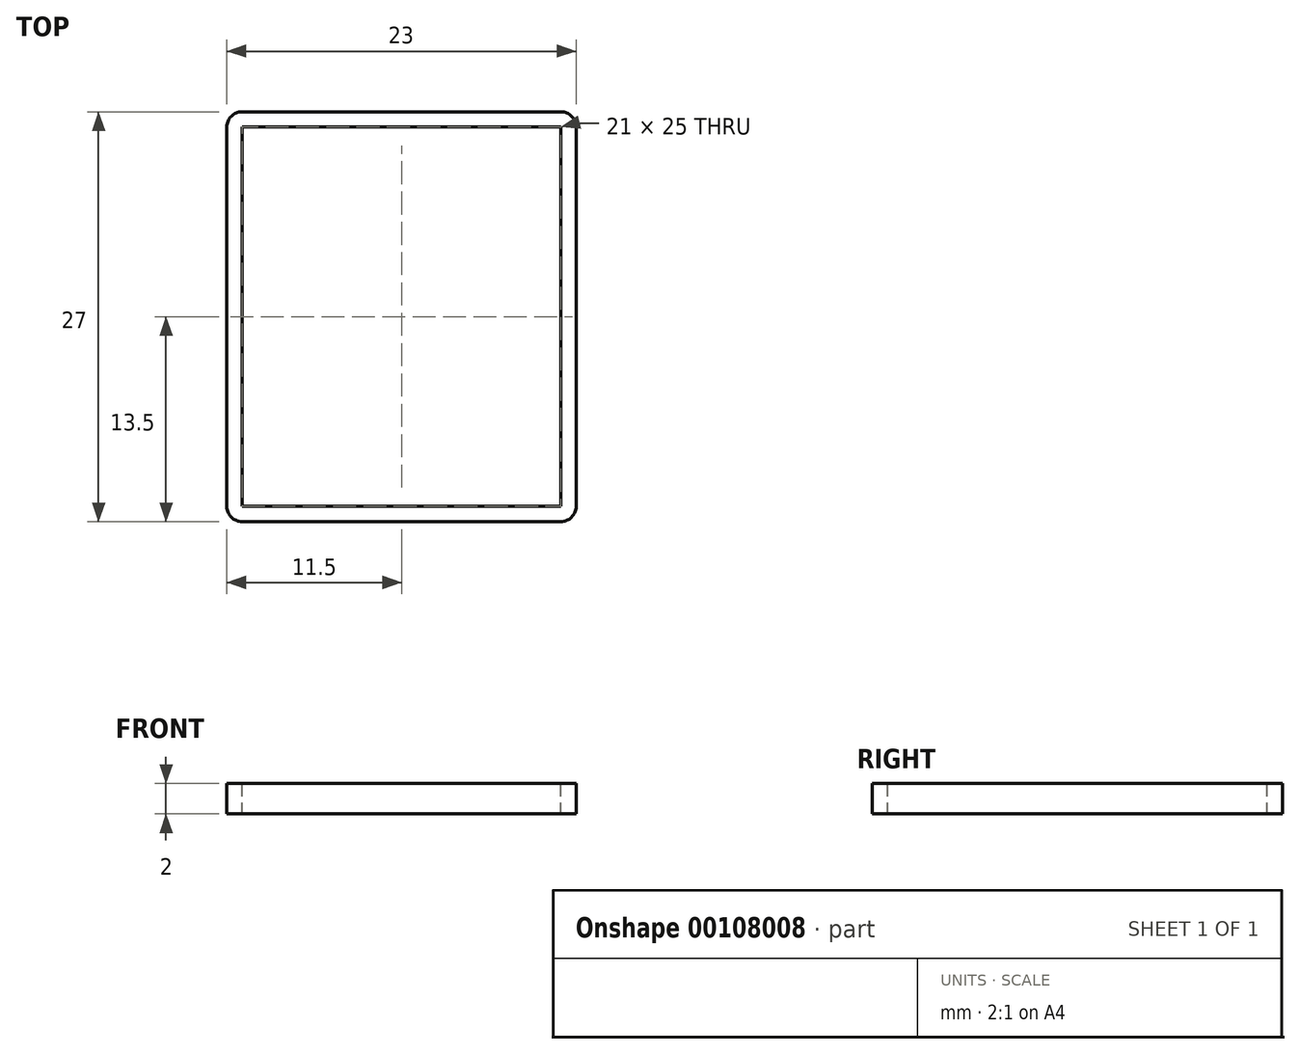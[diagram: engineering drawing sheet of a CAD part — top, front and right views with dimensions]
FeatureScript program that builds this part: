
annotation { "Feature Type Name" : "Feature", "Feature Type Description" : "" }
export const myFeature = defineFeature(function(context is Context, id is Id, definition is map)
    precondition{}
    {
        {
            var Q0;
            Q0=qCreatedBy(makeId("Top.planeOp"),FACE);
            var sketch = newSketch(context, id + "F0", { "sketchPlane" : qUnion([Q0])});
            skLineSegment(sketch, "E0.bottom", {"start": v(0, 0) * mm, "end": v(23, 0) * mm});
            skLineSegment(sketch, "E0.top", {"start": v(0, 27) * mm, "end": v(23, 27) * mm});
            skLineSegment(sketch, "E0.left", {"start": v(0, 0) * mm, "end": v(0, 27) * mm});
            skLineSegment(sketch, "E0.right", {"start": v(23, 0) * mm, "end": v(23, 27) * mm});
            skSolve(sketch);
        }
        {
            var Q0;
            Q0=makeQuery(id+"F0.imprint","IMPRINT",FACE,{"disambiguationData":[TD([[makeQuery(id+"F0.imprint","IMPRINT",EDGE,{"derivedFrom":sQuery(id+"F0.wireOp",EDGE,"E0.bottom")}),1.0]])]});
            extrude(context, id + "F1", {"entities" : qUnion([Q0]), "depth" : 2 * mm});
        }
        {
            var Q0;
            Q0=makeQuery(id+"F1.opExtrude","CAP_FACE",FACE,{"disambiguationData":[OSD([sQuery(id+"F0.wireOp",EDGE,"E0.bottom"),sQuery(id+"F0.wireOp",EDGE,"E0.top"),sQuery(id+"F0.wireOp",EDGE,"E0.left"),sQuery(id+"F0.wireOp",EDGE,"E0.right")])],"isStart":false});
            var sketch = newSketch(context, id + "F2", { "sketchPlane" : qUnion([Q0])});
            skLineSegment(sketch, "E1.bottom", {"start": v(1, 26) * mm, "end": v(22, 26) * mm});
            skLineSegment(sketch, "E1.top", {"start": v(1, 1) * mm, "end": v(22, 1) * mm});
            skLineSegment(sketch, "E1.left", {"start": v(1, 26) * mm, "end": v(1, 1) * mm});
            skLineSegment(sketch, "E1.right", {"start": v(22, 26) * mm, "end": v(22, 1) * mm});
            skPoint(sketch, "E1.middle", {"position": v(11.5, 13.5) * mm});
            skPoint(sketch, "E1.middle.positionSnap0", {"position": v(23, 13.5) * mm});
            skPoint(sketch, "E1.middle.positionSnap1", {"position": v(11.5, 27) * mm});
            skPoint(sketch, "E1.centerSnap0", {"position": v(23, 13.5) * mm});
            skPoint(sketch, "E1.centerSnap1", {"position": v(11.5, 27) * mm});
            skSolve(sketch);
        }
        {
            var Q0;
            Q0 = qSketchRegion(id + "F2", true);
            extrude(context, id + "F3", {"entities" : qUnion([Q0]), "operationType" : NewBodyOperationType.REMOVE, "endBound" : BoundingType.THROUGH_ALL, "oppositeDirection" : true, "depth" : 2 * mm});
        }
        {
            var Q0;
            Q0=makeQuery(id+"F1.opExtrude","SWEPT_EDGE",EDGE,{"disambiguationData":[OSD([sQuery(id+"F0.wireOp",EDGE,"E0.bottom"),sQuery(id+"F0.wireOp",EDGE,"E0.right")])]});
            var Q1;
            Q1=makeQuery(id+"F1.opExtrude","SWEPT_EDGE",EDGE,{"disambiguationData":[OSD([sQuery(id+"F0.wireOp",EDGE,"E0.top"),sQuery(id+"F0.wireOp",EDGE,"E0.right")])]});
            var Q2;
            Q2=makeQuery(id+"F1.opExtrude","SWEPT_EDGE",EDGE,{"disambiguationData":[OSD([sQuery(id+"F0.wireOp",EDGE,"E0.bottom"),sQuery(id+"F0.wireOp",EDGE,"E0.left")])]});
            var Q3;
            Q3=makeQuery(id+"F1.opExtrude","SWEPT_EDGE",EDGE,{"disambiguationData":[OSD([sQuery(id+"F0.wireOp",EDGE,"E0.top"),sQuery(id+"F0.wireOp",EDGE,"E0.left")])]});
            fillet(context, id + "F4", {"entities" : qUnion([Q0, Q1, Q2, Q3]), "radius" : 1 * mm, "tangentPropagation" : true, "allowEdgeOverflow" : false});
        }
    });
